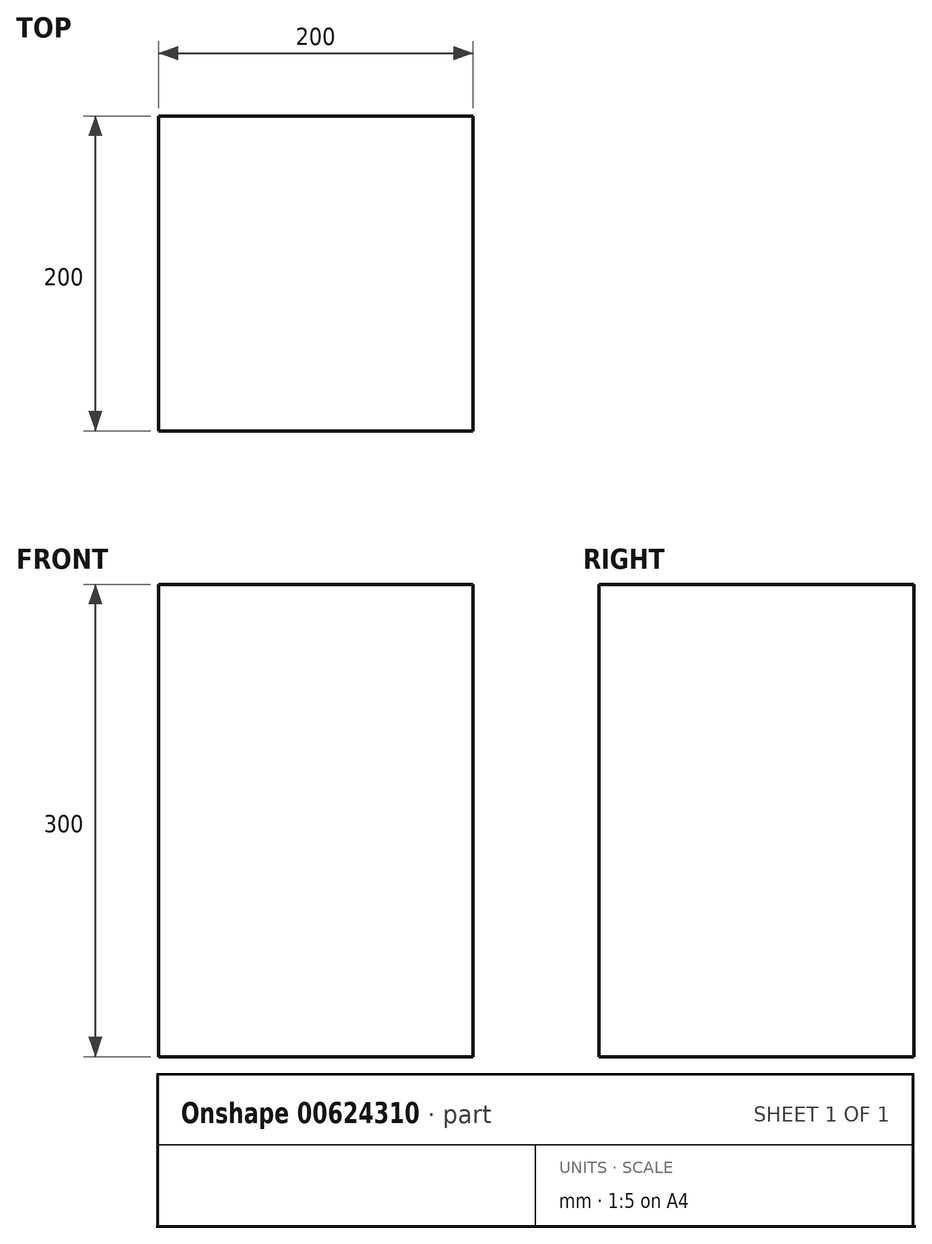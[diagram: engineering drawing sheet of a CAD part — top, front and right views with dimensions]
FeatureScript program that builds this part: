
annotation { "Feature Type Name" : "Feature", "Feature Type Description" : "" }
export const myFeature = defineFeature(function(context is Context, id is Id, definition is map)
    precondition{}
    {
        {
            var Q0;
            Q0=qCreatedBy(makeId("Top.planeOp"),FACE);
            var sketch = newSketch(context, id + "F0", { "sketchPlane" : qUnion([Q0])});
            skLineSegment(sketch, "E0.bottom", {"start": v(100, -100) * mm, "end": v(-100, -100) * mm});
            skLineSegment(sketch, "E0.top", {"start": v(100, 100) * mm, "end": v(-100, 100) * mm});
            skLineSegment(sketch, "E0.left", {"start": v(100, -100) * mm, "end": v(100, 100) * mm});
            skLineSegment(sketch, "E0.right", {"start": v(-100, -100) * mm, "end": v(-100, 100) * mm});
            skPoint(sketch, "E0.middle", {"position": v(0, 0) * mm});
            skSolve(sketch);
        }
        {
            var Q0;
            Q0=makeQuery(id+"F0.imprint","IMPRINT",FACE,{"disambiguationData":[TD([[makeQuery(id+"F0.imprint","IMPRINT",EDGE,{"derivedFrom":sQuery(id+"F0.wireOp",EDGE,"E0.bottom")}),-1.0]])]});
            extrude(context, id + "F1", {"entities" : qUnion([Q0]), "depth" : 300 * mm, "offsetDistance" : 25 * mm});
        }
    });
